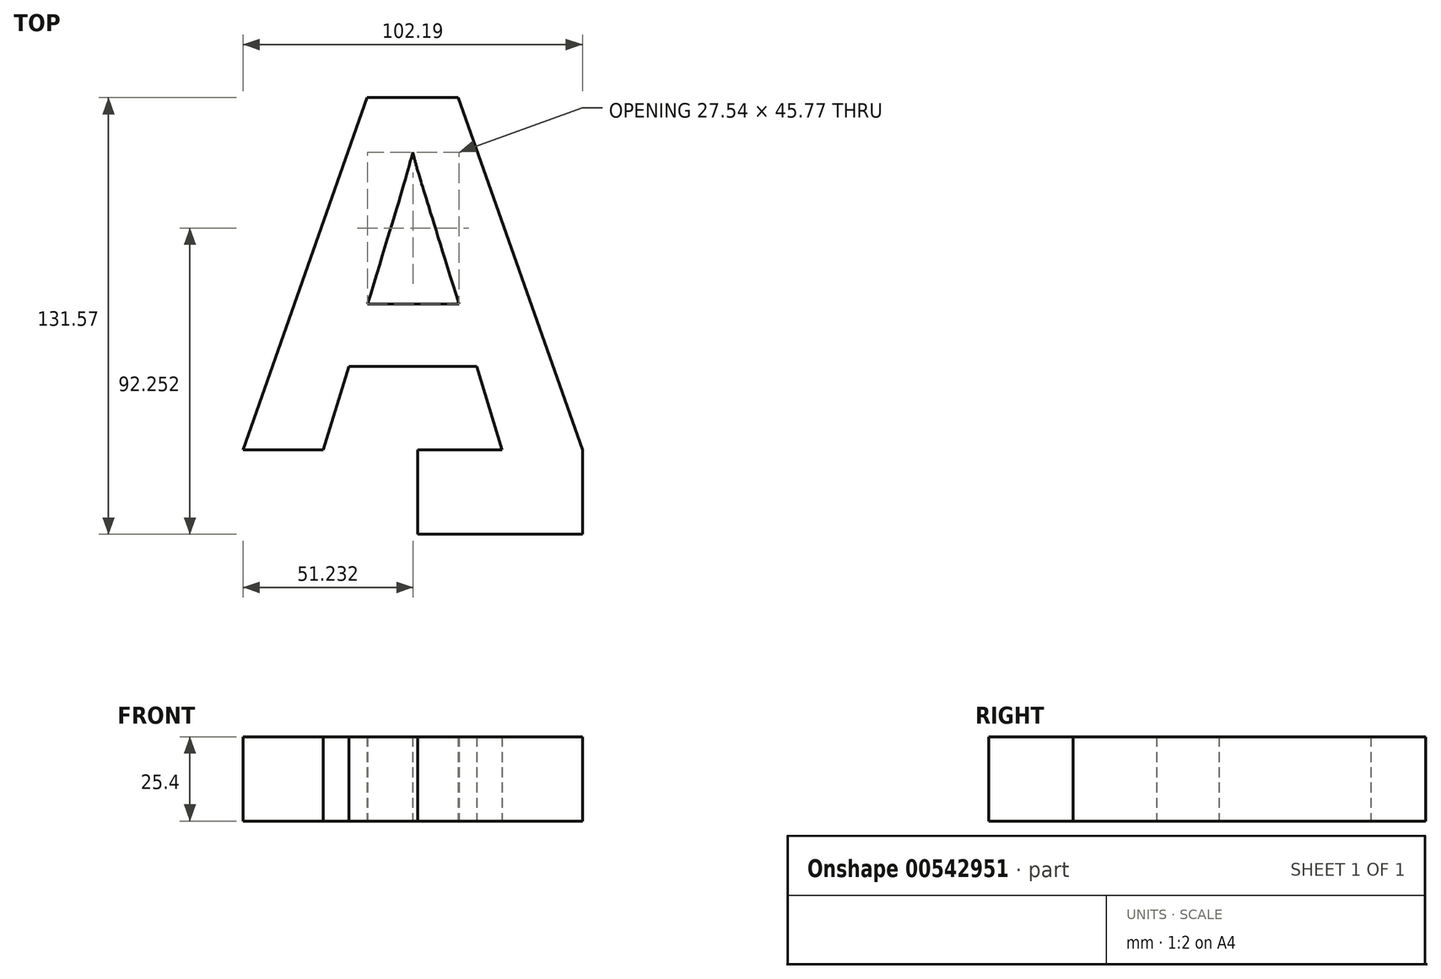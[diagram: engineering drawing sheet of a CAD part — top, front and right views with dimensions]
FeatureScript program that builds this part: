
annotation { "Feature Type Name" : "Feature", "Feature Type Description" : "" }
export const myFeature = defineFeature(function(context is Context, id is Id, definition is map)
    precondition{}
    {
        {
            var Q0;
            Q0=qCreatedBy(makeId("Top.planeOp"),FACE);
            var sketch = newSketch(context, id + "F0", { "sketchPlane" : qUnion([Q0])});
            skText(sketch, "E0", { "text": "A", "fontName": "OpenSans-Bold.ttf"});
            const initialGuessF0  = {"E0": [-0.14112, -0.05886, 1, 0, 0.10663]};
            skSetInitialGuess(sketch, initialGuessF0);
            skSolve(sketch);
        }
        {
            var Q0;
            Q0 = qSketchRegion(id + "F0", true);
            extrude(context, id + "F1", {"entities" : qUnion([Q0]), "depth" : 25.4 * mm, "offsetDistance" : 25.4 * mm});
        }
        {
            var Q0;
            Q0=makeQuery(id+"F1.opExtrude","SWEPT_FACE",FACE,{"disambiguationData":[OSD([sQuery(id+"F0.wireOp",EDGE,"E0.sketch_text.stroke-7")])]});
            extrude(context, id + "F2", {"entities" : qUnion([Q0]), "operationType" : NewBodyOperationType.ADD, "depth" : 25.4 * mm, "offsetDistance" : 25.4 * mm});
        }
        {
            var Q0;
            Q0=makeQuery(id+"F2.opExtrude","SWEPT_FACE",FACE,{"disambiguationData":[OSD([sQuery(id+"F0.wireOp",EDGE,"E0.sketch_text.stroke-0"),sQuery(id+"F0.wireOp",EDGE,"E0.sketch_text.stroke-7")])]});
            extrude(context, id + "F3", {"entities" : qUnion([Q0]), "operationType" : NewBodyOperationType.ADD, "depth" : 25.4 * mm, "offsetDistance" : 25.4 * mm});
        }
    });
